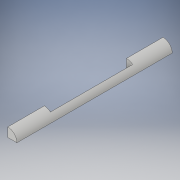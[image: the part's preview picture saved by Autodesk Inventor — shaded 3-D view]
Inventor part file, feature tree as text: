
AUTODESK INVENTOR PART (.ipt)
format: ipt  version: 2019.1 (Build 231200000, 200)  size: 107,520 bytes
history: native  units: in
note: dims shown in document units (in); Inventor stores cm internally (conversion verified against a paired STEP export)
features: extrude x2, sketch x2
ambient origin geometry x8: Origin, YZ Plane, XZ Plane, XY Plane, X Axis, Y Axis, Z Axis, Center Point
bodies: Solid1 (feature_tree)
feature tree (4):
  extrude  "Extrusion1"  Depth=6.375in TaperAngle=0.0deg
  extrude  "Extrusion2"  Depth=1.5in
  sketch  "Sketch1"  dims[d0=0.75in d1=6.375in d2=0.0in]
  sketch  "Sketch2"  dims[d3=3.375in d4=1.5in d5=0.25in d6=0.0in d7=0.0in]
